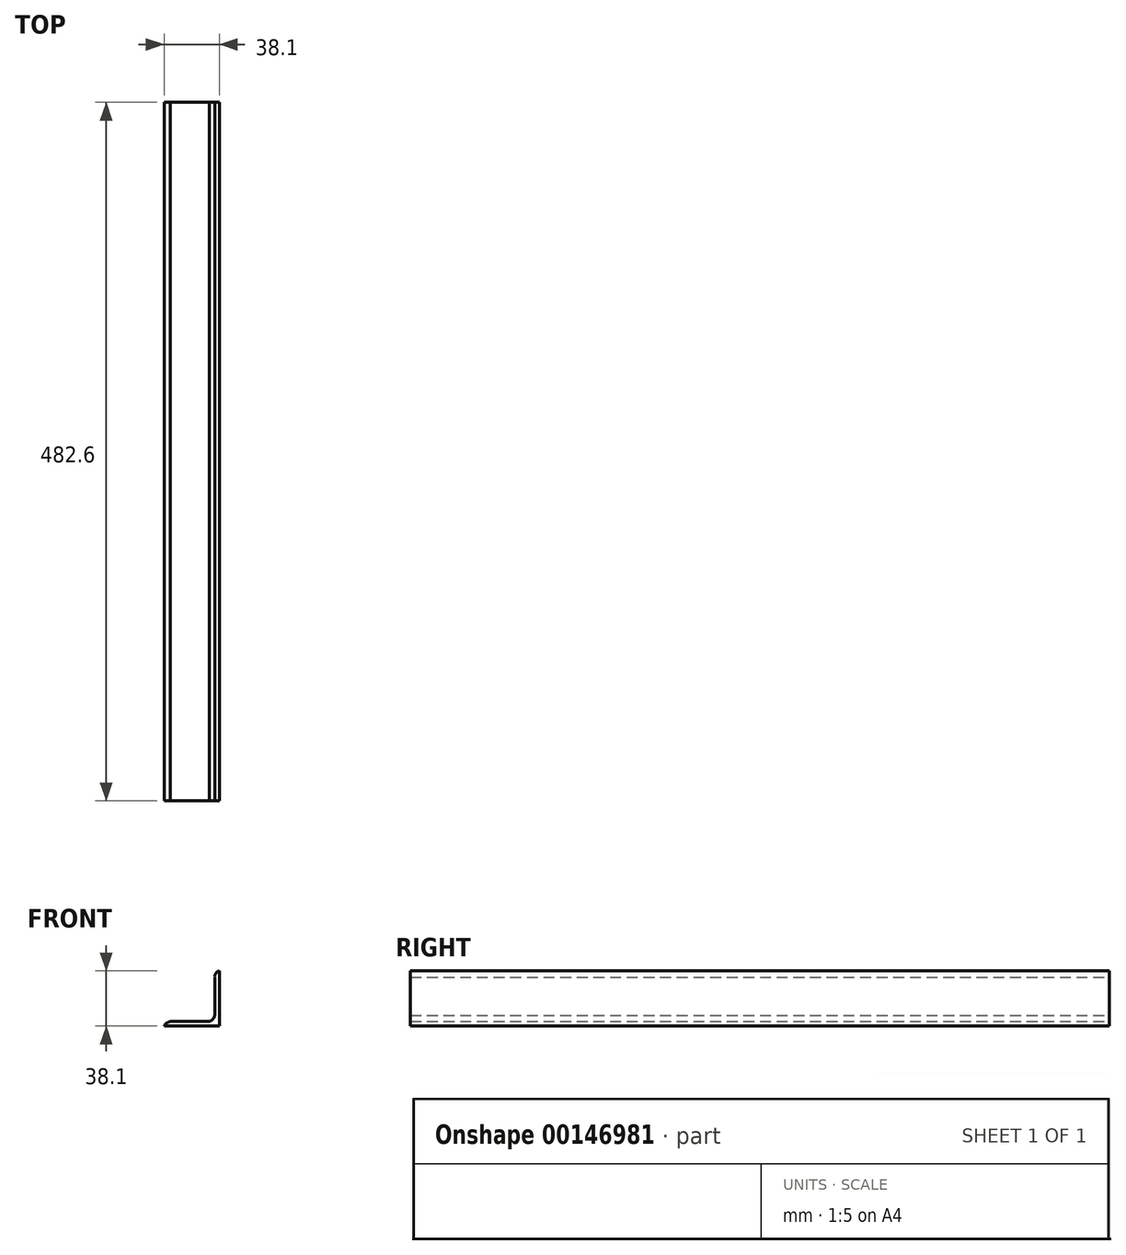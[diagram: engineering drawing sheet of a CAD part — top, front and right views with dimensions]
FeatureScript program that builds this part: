
annotation { "Feature Type Name" : "Feature", "Feature Type Description" : "" }
export const myFeature = defineFeature(function(context is Context, id is Id, definition is map)
    precondition{}
    {
        {
            var Q0;
            Q0=qCreatedBy(makeId("Front.planeOp"),FACE);
            var sketch = newSketch(context, id + "F0", { "sketchPlane" : qUnion([Q0])});
            skLineSegment(sketch, "E0.bottom", {"start": v(0, 0) * mm, "end": v(-3.18, 0) * mm});
            skLineSegment(sketch, "E0.left", {"start": v(0, 0) * mm, "end": v(0, 38.1) * mm});
            skLineSegment(sketch, "E0.right", {"start": v(-3.18, 7.32) * mm, "end": v(-3.18, 33.64) * mm});
            skLineSegment(sketch, "E1.bottom", {"start": v(0, 0) * mm, "end": v(-38.1, 0) * mm});
            skLineSegment(sketch, "E1.top", {"start": v(-6.72, 3.18) * mm, "end": v(-33.88, 3.17) * mm});
            skLineSegment(sketch, "E1.left", {"start": v(0, 0) * mm, "end": v(0, 3.18) * mm});
            skArc(sketch, "E2", {"start": v(-33.88, 3.17) * mm, "mid": v(-36.36, 2.09) * mm, "end": v(-38.1, 0) * mm});
            skArc(sketch, "E3", {"start": v(0, 38.1) * mm, "mid": v(-2.37, 36.43) * mm, "end": v(-3.18, 33.64) * mm});
            skArc(sketch, "E4", {"start": v(-6.72, 3.18) * mm, "mid": v(-4.42, 4.8) * mm, "end": v(-3.18, 7.32) * mm});
            skSolve(sketch);
        }
        {
            var Q0;
            Q0 = qSketchRegion(id + "F0", true);
            extrude(context, id + "F1", {"entities" : qUnion([Q0]), "depth" : 482.6 * mm});
        }
    });
